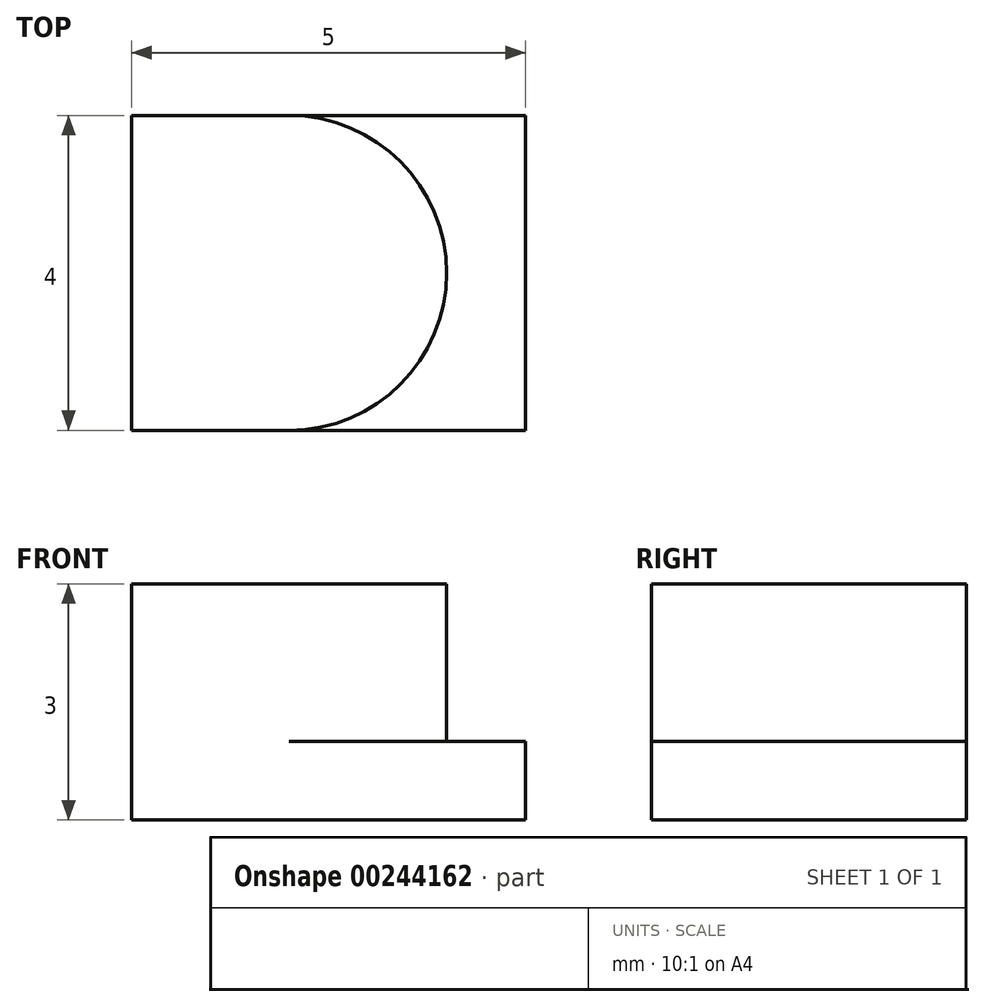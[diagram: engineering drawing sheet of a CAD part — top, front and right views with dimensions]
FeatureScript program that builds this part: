
annotation { "Feature Type Name" : "Feature", "Feature Type Description" : "" }
export const myFeature = defineFeature(function(context is Context, id is Id, definition is map)
    precondition{}
    {
        {
            var Q0;
            Q0=qCreatedBy(makeId("Top.planeOp"),FACE);
            var sketch = newSketch(context, id + "F0", { "sketchPlane" : qUnion([Q0])});
            skLineSegment(sketch, "E0.bottom", {"start": v(0, 0) * mm, "end": v(5, 0) * mm});
            skLineSegment(sketch, "E0.top", {"start": v(0, 4) * mm, "end": v(5, 4) * mm});
            skLineSegment(sketch, "E0.left", {"start": v(0, 0) * mm, "end": v(0, 4) * mm});
            skLineSegment(sketch, "E0.right", {"start": v(5, 0) * mm, "end": v(5, 4) * mm});
            skSolve(sketch);
        }
        {
            var Q0;
            Q0 = qSketchRegion(id + "F0", true);
            extrude(context, id + "F1", {"entities" : qUnion([Q0]), "depth" : 1 * mm});
        }
        {
            var Q0;
            Q0=makeQuery(id+"F1.opExtrude","CAP_FACE",FACE,{"disambiguationData":[OSD([sQuery(id+"F0.wireOp",EDGE,"E0.bottom"),sQuery(id+"F0.wireOp",EDGE,"E0.top"),sQuery(id+"F0.wireOp",EDGE,"E0.left"),sQuery(id+"F0.wireOp",EDGE,"E0.right")])],"isStart":false});
            var sketch = newSketch(context, id + "F2", { "sketchPlane" : qUnion([Q0])});
            skLineSegment(sketch, "E1", {"start": v(0, 2) * mm, "end": v(2, 2) * mm, "construction": true});
            skArc(sketch, "E2", {"start": v(2, 0) * mm, "mid": v(4, 2) * mm, "end": v(2, 4) * mm});
            skLineSegment(sketch, "E3.0", {"start": v(0, 4) * mm, "end": v(2, 4) * mm});
            skLineSegment(sketch, "E3.1", {"start": v(0, 0) * mm, "end": v(2, 0) * mm});
            skLineSegment(sketch, "E3.2", {"start": v(0, 0) * mm, "end": v(0, 4) * mm});
            skSolve(sketch);
        }
        {
            var Q0;
            Q0 = qSketchRegion(id + "F2", true);
            extrude(context, id + "F3", {"entities" : qUnion([Q0]), "operationType" : NewBodyOperationType.ADD, "depth" : 2 * mm});
        }
    });
